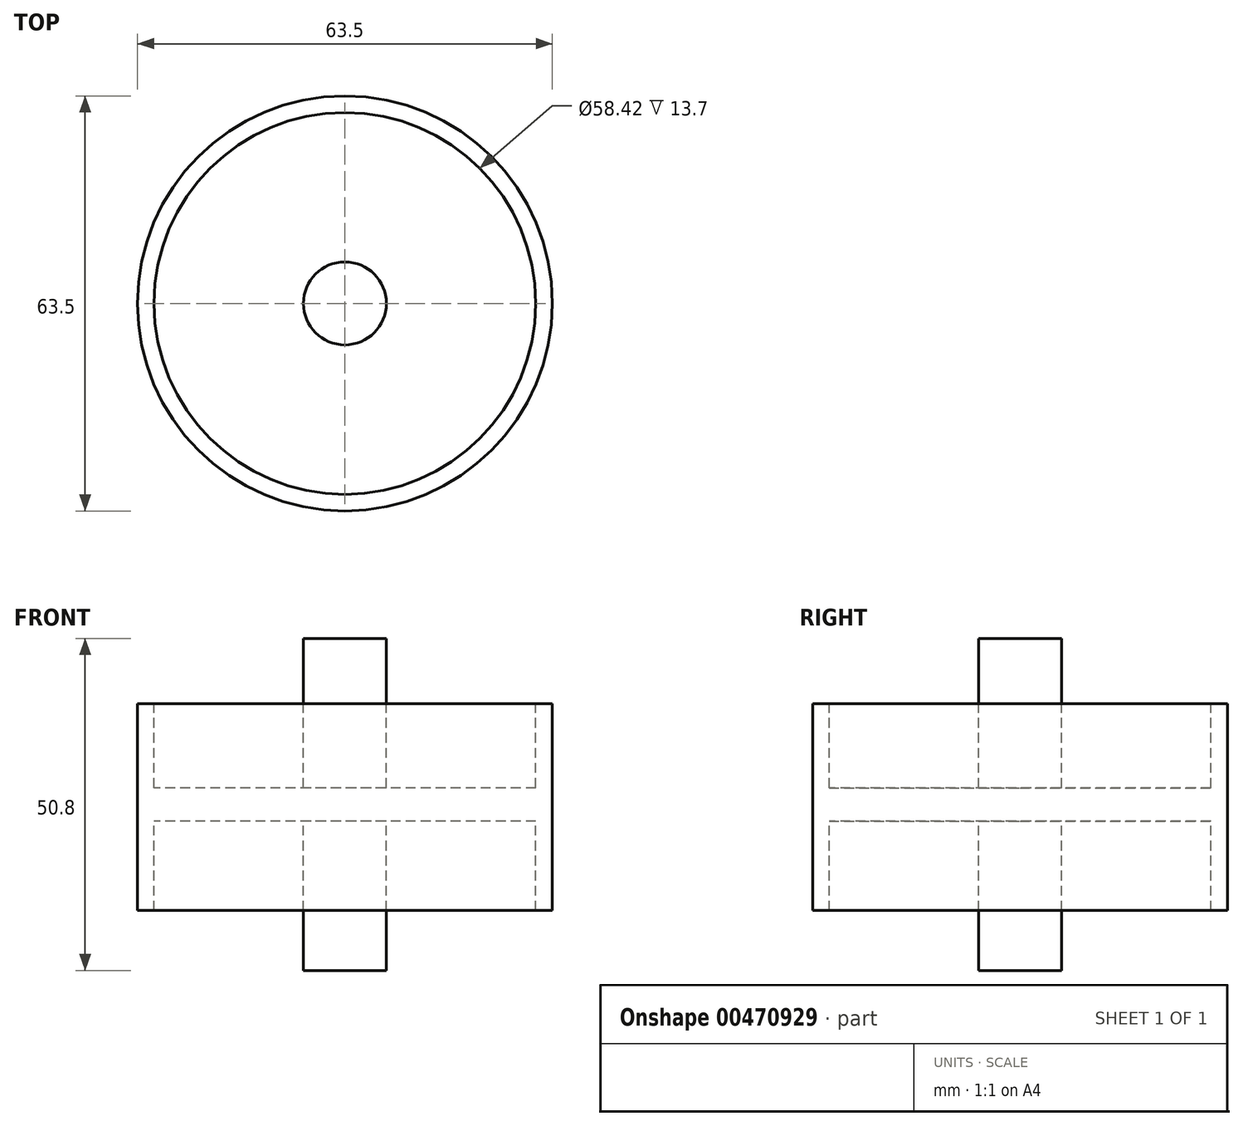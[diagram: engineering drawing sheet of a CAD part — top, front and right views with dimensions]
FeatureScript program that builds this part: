
annotation { "Feature Type Name" : "Feature", "Feature Type Description" : "" }
export const myFeature = defineFeature(function(context is Context, id is Id, definition is map)
    precondition{}
    {
        {
            var Q0;
            Q0=qCreatedBy(makeId("Front.planeOp"),FACE);
            var sketch = newSketch(context, id + "F0", { "sketchPlane" : qUnion([Q0])});
            skLineSegment(sketch, "E0", {"start": v(0, 25.1) * mm, "end": v(0, -25.7) * mm});
            skLineSegment(sketch, "E1", {"start": v(0, -25.7) * mm, "end": v(6.35, -25.7) * mm});
            skLineSegment(sketch, "E2", {"start": v(6.35, -25.7) * mm, "end": v(6.35, -11.73) * mm});
            skLineSegment(sketch, "E3", {"start": v(6.35, -11.73) * mm, "end": v(29.21, -11.73) * mm});
            skLineSegment(sketch, "E4", {"start": v(29.21, -11.73) * mm, "end": v(29.21, 11.13) * mm});
            skLineSegment(sketch, "E5", {"start": v(29.21, 11.13) * mm, "end": v(6.35, 11.13) * mm});
            skLineSegment(sketch, "E6", {"start": v(6.35, 11.13) * mm, "end": v(6.35, 25.1) * mm});
            skLineSegment(sketch, "E7", {"start": v(6.35, 25.1) * mm, "end": v(0, 25.1) * mm});
            skLineSegment(sketch, "E8", {"start": v(29.21, 11.13) * mm, "end": v(29.21, 15.12) * mm});
            skLineSegment(sketch, "E9", {"start": v(29.21, 15.12) * mm, "end": v(31.75, 15.12) * mm});
            skLineSegment(sketch, "E10", {"start": v(31.75, 15.12) * mm, "end": v(31.75, -16.54) * mm});
            skLineSegment(sketch, "E11", {"start": v(31.75, -16.54) * mm, "end": v(29.21, -16.54) * mm});
            skLineSegment(sketch, "E12", {"start": v(29.21, -16.54) * mm, "end": v(29.21, -11.73) * mm});
            skSolve(sketch);
        }
        {
            var Q0;
            Q0=makeQuery(id+"F0.imprint","IMPRINT",FACE,{"disambiguationData":[TD([[makeQuery(id+"F0.imprint","IMPRINT",EDGE,{"derivedFrom":sQuery(id+"F0.wireOp",EDGE,"E4")}),-1.0]])]});
            var Q1;
            Q1=makeQuery(id+"F0.imprint","IMPRINT",FACE,{"disambiguationData":[TD([[makeQuery(id+"F0.imprint","IMPRINT",EDGE,{"derivedFrom":sQuery(id+"F0.wireOp",EDGE,"E0")}),1.0]])]});
            var Q2;
            Q2=sQuery(id+"F0.wireOp",EDGE,"E0");
            revolve(context, id + "F1", {"entities" : qUnion([Q0, Q1]), "axis" : qUnion([Q2]), "revolveType" : RevolveType.FULL});
        }
        {
            var Q0;
            Q0=makeQuery(id+"F1.opRevolve","SWEPT_FACE",FACE,{"disambiguationData":[OSD([sQuery(id+"F0.wireOp",EDGE,"E5")])]});
            extrude(context, id + "F2", {"entities" : qUnion([Q0]), "operationType" : NewBodyOperationType.REMOVE, "oppositeDirection" : true, "depth" : 8.9 * mm});
        }
        {
            var Q0;
            Q0=makeQuery(id+"F1.opRevolve","SWEPT_FACE",FACE,{"disambiguationData":[OSD([sQuery(id+"F0.wireOp",EDGE,"E3")])]});
            extrude(context, id + "F3", {"entities" : qUnion([Q0]), "operationType" : NewBodyOperationType.REMOVE, "oppositeDirection" : true, "depth" : 8.9 * mm});
        }
    });
